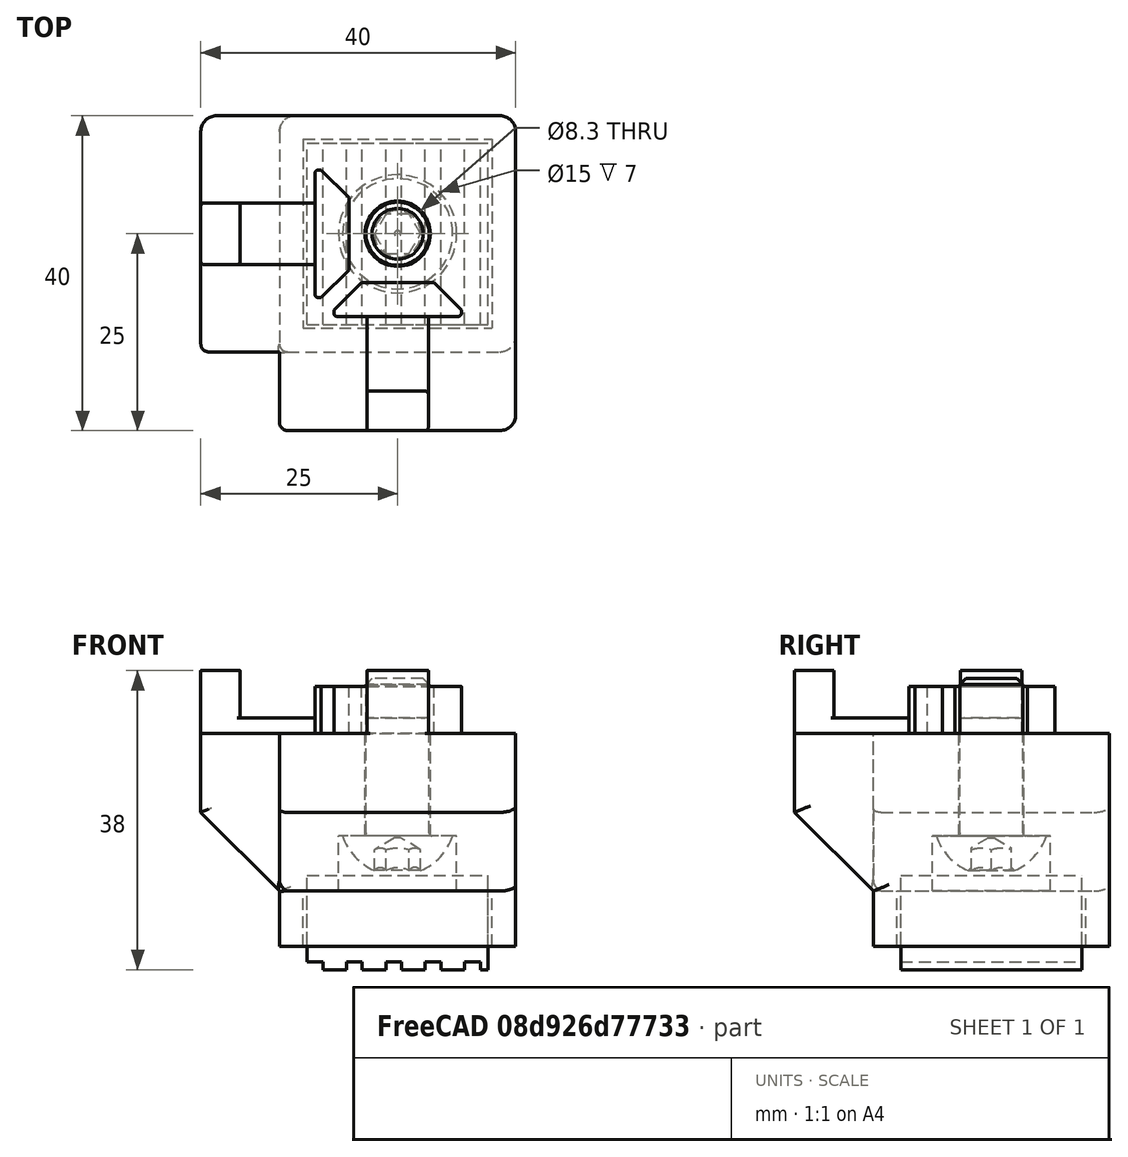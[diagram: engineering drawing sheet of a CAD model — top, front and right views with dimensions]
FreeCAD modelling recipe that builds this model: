
FCSTD DOCUMENT  (FreeCAD 0.19R24291 (Git))
Label: foot-assembly
License: Other
LicenseURL: GPL3
objects: Part::Feature×2, Spreadsheet::Sheet×2, PartDesign::CoordinateSystem×1, Part::FeaturePython×1, App::Part×1
note: 4 computed .brp shape members not serialized (recipe doc carries the construction recipe); baked Part::Feature solids carry a one-line shape summary decoded from their .brp

FEATURE [Part::Feature] Cut002002001001  label="rubber24x24x10"
  shape: bbox 23 x 23 x 12 mm, 24 faces (baked)
FEATURE [Part::Feature] Cut002003001001  label="foot-corner"
  shape: bbox 40.3 x 40.3 x 35.3 mm, 68 faces (baked)
FEATURE [PartDesign::CoordinateSystem] LCS_foot
  AttacherType = Attacher::AttachEngine3D
FEATURE [Part::FeaturePython] Screw  label="M8x20-Screw"  # Fasteners workbench fastener (typed FeaturePython)
  Placement = pos=(0,0,17) rot=(-1,0,0;3.14159rad)
  baseObject = -> Cut002003001001 [Edge127]
  diameter = 5
  invert = true
  length = 3
  lengthCustom = 20
  matchOuter = false
  offset = 0
  thread = false
  type = 40
FEATURE [App::Part] Part  label="foot"
  Group = -> [Cut002003001001,Cut002002001001,LCS_foot,Screw]
  Origin = -> Origin
FEATURE [Spreadsheet::Sheet] Fasteners_BOM
  cells = A1=Type; B1=Qty; A2=ISO7380-1 Screw M10x25; B2=5
FEATURE [Spreadsheet::Sheet] Fasteners_BOM001
  cells = A1=Type; B1=Qty; A2=ISO7380-1 Screw M10x25; B2=5
